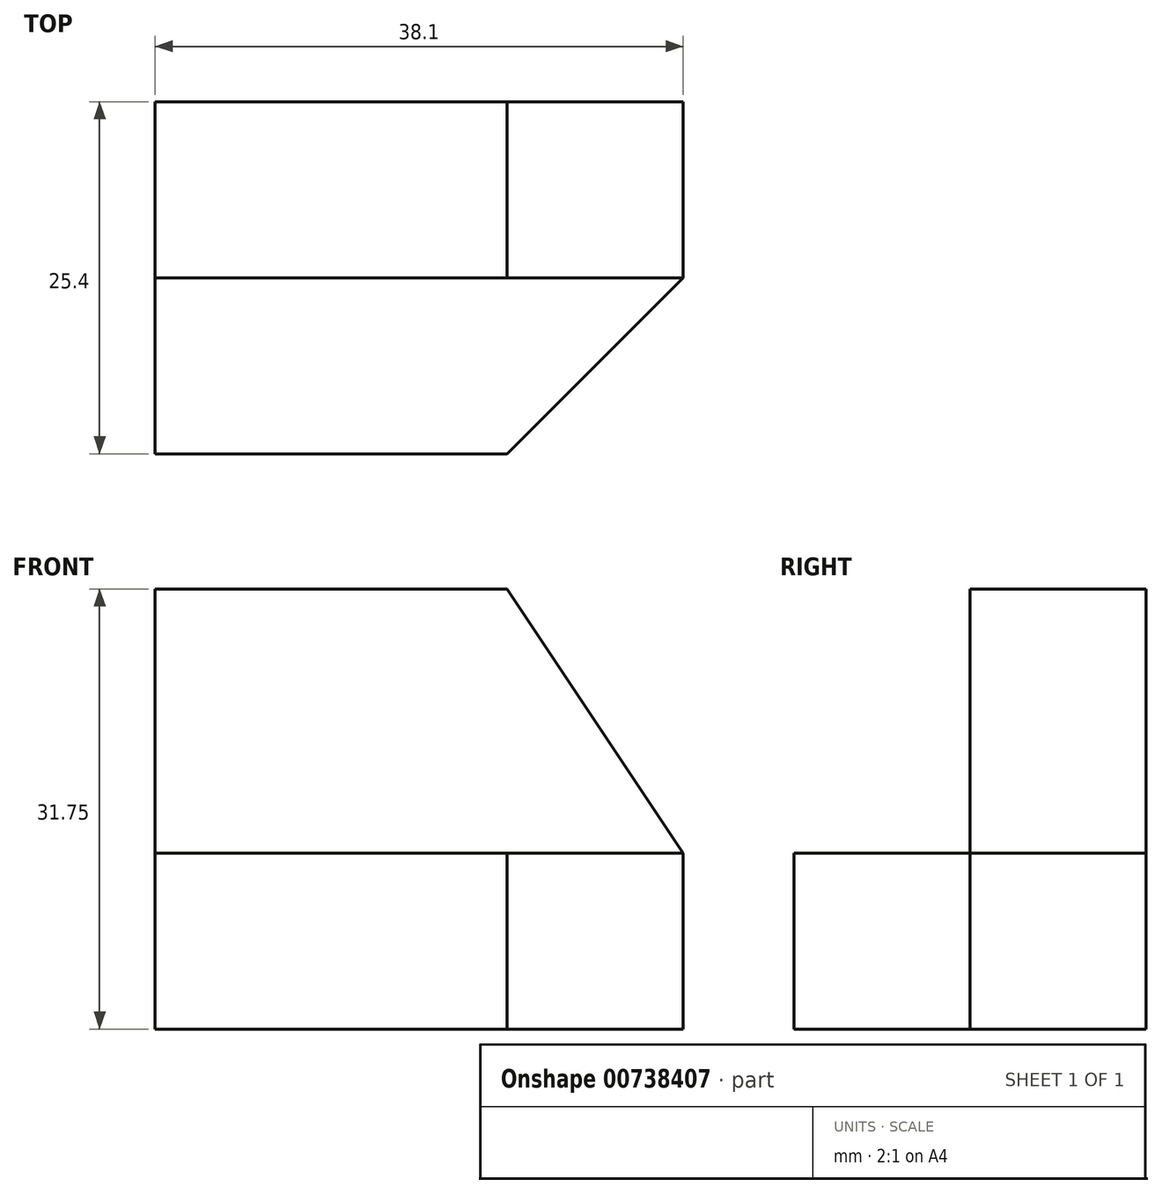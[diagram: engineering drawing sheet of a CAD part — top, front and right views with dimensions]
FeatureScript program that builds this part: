
annotation { "Feature Type Name" : "Feature", "Feature Type Description" : "" }
export const myFeature = defineFeature(function(context is Context, id is Id, definition is map)
    precondition{}
    {
        {
            var Q0;
            Q0=qCreatedBy(makeId("Top.planeOp"),FACE);
            var sketch = newSketch(context, id + "F0", { "sketchPlane" : qUnion([Q0])});
            skLineSegment(sketch, "E0.bottom", {"start": v(0, 0) * mm, "end": v(38.1, 0) * mm});
            skLineSegment(sketch, "E0.top", {"start": v(0, 25.4) * mm, "end": v(38.1, 25.4) * mm});
            skLineSegment(sketch, "E0.left", {"start": v(0, 0) * mm, "end": v(0, 25.4) * mm});
            skLineSegment(sketch, "E0.right", {"start": v(38.1, 0) * mm, "end": v(38.1, 25.4) * mm});
            skSolve(sketch);
        }
        {
            var Q0;
            Q0 = qSketchRegion(id + "F0", true);
            extrude(context, id + "F1", {"entities" : qUnion([Q0]), "depth" : 31.75 * mm, "offsetDistance" : 25.4 * mm});
        }
        {
            var Q0;
            Q0=makeQuery(id+"F1.opExtrude","SWEPT_FACE",FACE,{"disambiguationData":[OSD([sQuery(id+"F0.wireOp",EDGE,"E0.right")])]});
            var sketch = newSketch(context, id + "F2", { "sketchPlane" : qUnion([Q0])});
            skLineSegment(sketch, "E1.bottom", {"start": v(0, 31.75) * mm, "end": v(12.7, 31.75) * mm});
            skLineSegment(sketch, "E1.top", {"start": v(0, 12.7) * mm, "end": v(12.7, 12.7) * mm});
            skLineSegment(sketch, "E1.left", {"start": v(0, 31.75) * mm, "end": v(0, 12.7) * mm});
            skLineSegment(sketch, "E1.right", {"start": v(12.7, 31.75) * mm, "end": v(12.7, 12.7) * mm});
            skSolve(sketch);
        }
        {
            var Q0;
            Q0=makeQuery(id+"F2.imprint","IMPRINT",FACE,{"disambiguationData":[TD([[makeQuery(id+"F2.imprint","IMPRINT",EDGE,{"derivedFrom":sQuery(id+"F2.wireOp",EDGE,"E1.bottom")}),-1.0]])]});
            extrude(context, id + "F3", {"entities" : qUnion([Q0]), "operationType" : NewBodyOperationType.REMOVE, "oppositeDirection" : true, "depth" : 50.8 * mm, "offsetDistance" : 25.4 * mm});
        }
        {
            var Q0;
            Q0=makeQuery(id+"F3.boolean.opBoolean","COPY",FACE,{"derivedFrom":makeQuery(id+"F3.opExtrude","SWEPT_FACE",FACE,{"disambiguationData":[OSD([sQuery(id+"F2.wireOp",EDGE,"E1.right")])]})});
            var sketch = newSketch(context, id + "F4", { "sketchPlane" : qUnion([Q0])});
            skLineSegment(sketch, "E2", {"start": v(25.4, 31.75) * mm, "end": v(38.1, 12.7) * mm});
            skLineSegment(sketch, "E3", {"start": v(38.1, 12.7) * mm, "end": v(38.1, 31.75) * mm});
            skLineSegment(sketch, "E4", {"start": v(38.1, 31.75) * mm, "end": v(25.4, 31.75) * mm});
            skSolve(sketch);
        }
        {
            var Q0;
            Q0 = qSketchRegion(id + "F4", true);
            extrude(context, id + "F5", {"entities" : qUnion([Q0]), "operationType" : NewBodyOperationType.REMOVE, "oppositeDirection" : true, "depth" : 25.4 * mm, "offsetDistance" : 25.4 * mm});
        }
        {
            var Q0;
            Q0=makeQuery(id+"F3.boolean.opBoolean","COPY",FACE,{"derivedFrom":makeQuery(id+"F3.opExtrude","SWEPT_FACE",FACE,{"disambiguationData":[OSD([sQuery(id+"F2.wireOp",EDGE,"E1.top")])]})});
            var sketch = newSketch(context, id + "F6", { "sketchPlane" : qUnion([Q0])});
            skLineSegment(sketch, "E5", {"start": v(38.1, 12.7) * mm, "end": v(25.4, 0) * mm});
            skLineSegment(sketch, "E6", {"start": v(25.4, 0) * mm, "end": v(38.1, 0) * mm});
            skLineSegment(sketch, "E7", {"start": v(38.1, 0) * mm, "end": v(38.1, 12.7) * mm});
            skSolve(sketch);
        }
        {
            var Q0;
            Q0 = qSketchRegion(id + "F6", true);
            extrude(context, id + "F7", {"entities" : qUnion([Q0]), "operationType" : NewBodyOperationType.REMOVE, "oppositeDirection" : true, "depth" : 25.4 * mm, "offsetDistance" : 25.4 * mm});
        }
    });
